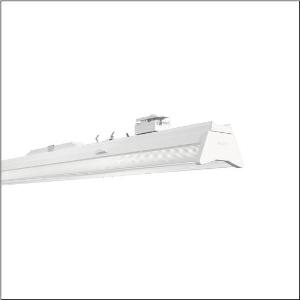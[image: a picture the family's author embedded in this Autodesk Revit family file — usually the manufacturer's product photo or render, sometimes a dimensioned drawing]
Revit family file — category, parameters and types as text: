
# Revit family: licross_r__21_performance_mo_52tm16cn46xg_6fd6
name_source: partatom
category: Lighting Fixtures
units: mm (PartAtom-declared; Revit-internal decimal feet)

## family parameters
Cut with Voids When Loaded = No
Host = Face
Light Source = No
Part Type = Normal
Room Calculation Point = No
Round Connector Dimension = Use Diameter
Shared = No

## types (1)
- --- (1 x LED, 6000 lm, 32 W, 4000K)
    Apparent Load = 32 VA
    CIE Flux Codes = 66 88 96 79 100
    Color Rendering = 80
    Color Temperature = 4000K
    Default Elevation = 1800 mm
    Description = Licross® 21 Performance MO, luminaire insert, of sheet steel, galvanised, coil coated, white, length: 1.500mm, width: 120mm, height: 123mm, LED rated luminous flux: 6.000lm, light colour: 840, control gear: ON/OFF Multilumen, CLOi, control gear: ECG Multilumen, with plug, 3-pole, with phase selection, mains connection: 220..240V, AC, 50/60Hz, start of lifetime: 32W, end of service life: 38W, halogen-free wiring, primary light control with lens, of plastic, primary optical cover: cover, of PMMA, light emission: direct/indirect distribution, primary light characteristic: symmetric, protection rating (complete): IP40, insulation class (complete): insulation class I (protective earthing), certification: CE, ENEC, UKCA, protection symbol: D if used in an environment without relevant dust loads with corresponding accessories, impact resistance: IK06, permissible ambient temperature for indoor applications: -35..+55°C, corresponds to IFS (International Featured Standards) requirements for safety and quality in the food industry, reducing of maximum allowable ambient temperature of 5°C with ceiling mounting, LABS conformity tested according to VDMA 24364:2018-05, packaging unit: 1 piece
    Height = 114 mm
    Lamp = 1 x LED
    Lamp Light Flux = 6000 lm
    Lamp Power = 32 W
    Lamp count = 1
    Length = 1500 mm
    Luminous efficacy = 188 lm/W
    Manufacturer = Siteco
    ModVariant = No
    Model = 52TM16CN46XG
    Mounting Place = Ceiling
    Mounting Type = Pendant
    Number of Poles = 1
    OnlyDefault = Yes
    Power Factor = 1
    Product Name = Licross® 21 Performance MO
    Product group = luminaire insert
    ProductGroupID = 901
    Protection Class = Protection class I
    Protection Degree = IP 40
    RLX_Detail_Level = 1
    RLX_Emergency_Light_Flux = 0 lm
    RLX_Emergency_Type = 0
    RLX_Emergency_Type_DB = No
    RlxData = <blob elided: 31833 chars, md5=c84e5322>
    Socket = socket
    Standby Power = 0 W
    System Light Flux = 6000 lm
    System Power = 32 W
    Type Comments = factory setting: luminous flux: 100 % | (A | C | E) | 74 mA
    Type Image = l_1256138.jpg
    URL = http://relux.com
    VarID = @adj_041665
    Voltage = 0 V
    Weight = 0.00 kg
    Width = 120 mm

## geometry (parser evidence)
native form markers: Blend x4, Sweep x11
no freeform markers — native parametric forms only
